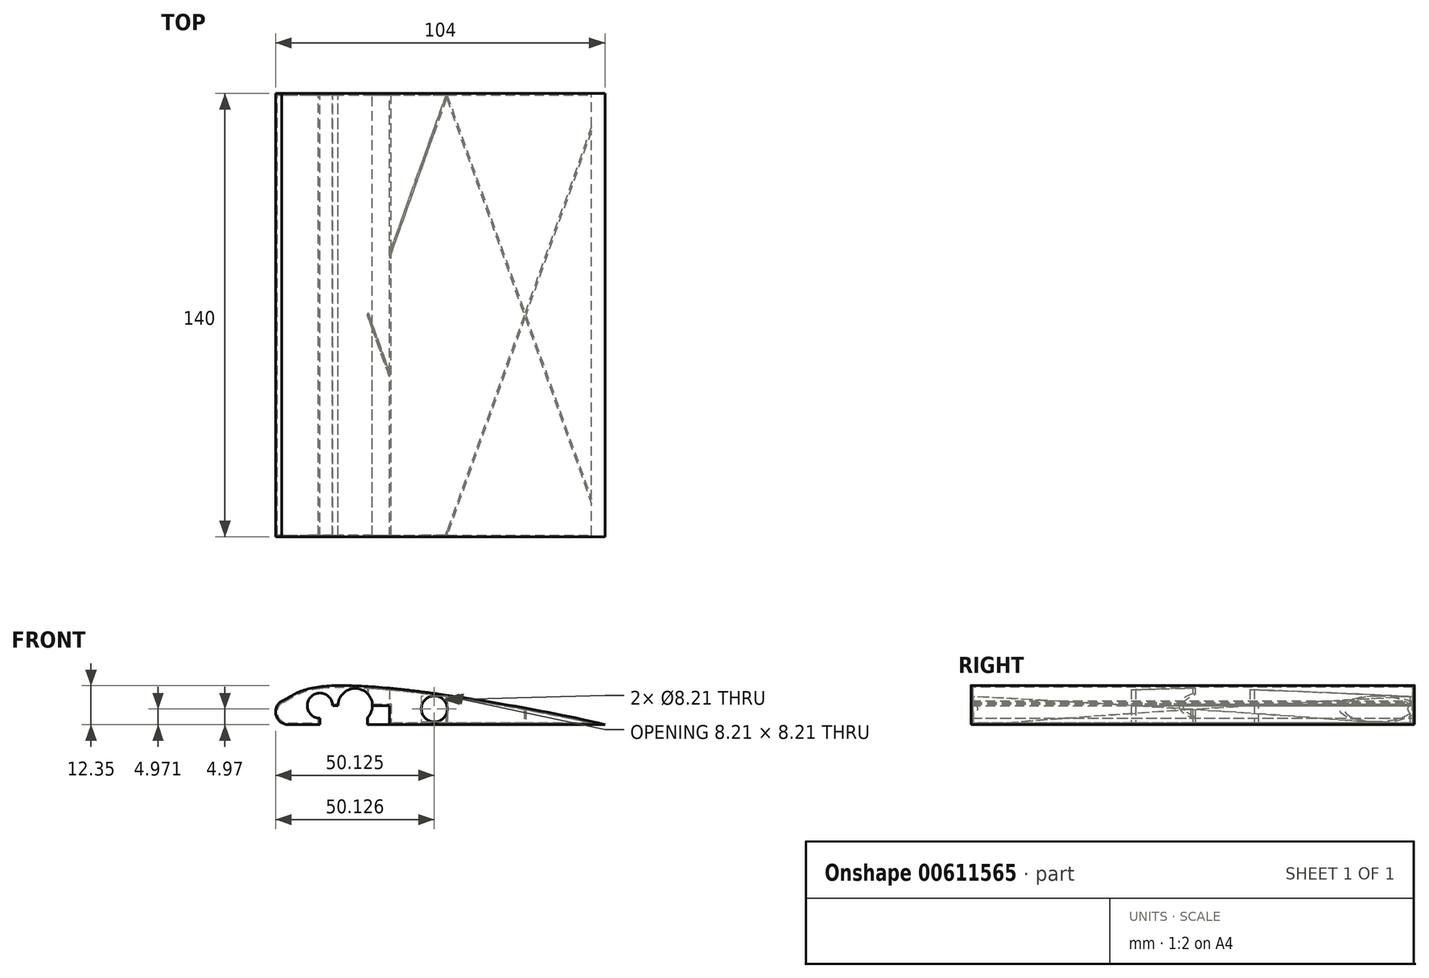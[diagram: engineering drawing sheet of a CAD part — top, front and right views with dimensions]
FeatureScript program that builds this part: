
annotation { "Feature Type Name" : "Feature", "Feature Type Description" : "" }
export const myFeature = defineFeature(function(context is Context, id is Id, definition is map)
    precondition{}
    {
        {
            var Q0;
            Q0=qCreatedBy(makeId("Front.planeOp"),FACE);
            var sketch = newSketch(context, id + "F0", { "sketchPlane" : qUnion([Q0])});
            skLineSegment(sketch, "E0", {"start": v(8.9, -4) * mm, "end": v(18.9, -4) * mm});
            skLineSegment(sketch, "E1", {"start": v(18.9, -4) * mm, "end": v(44.5, -4) * mm});
            skLineSegment(sketch, "E2", {"start": v(8.9, -4) * mm, "end": v(8.9, 4) * mm});
            skLineSegment(sketch, "E3", {"start": v(18.9, -4) * mm, "end": v(18.9, 8) * mm});
            skLineSegment(sketch, "E4", {"start": v(8.9, -4) * mm, "end": v(8.9, 0) * mm});
            skArc(sketch, "E5", {"start": v(8.9, -4) * mm, "mid": v(5.04, -1.04) * mm, "end": v(6.9, 3.46) * mm});
            skFitSpline(sketch, "E6", {"points": [v(6.9, 3.46) * mm, v(18.9, 8) * mm, v(108.9, -4) * mm], "startDerivative": vector(25.72, 9) * mm, "endDerivative": vector(55.93, -14.48) * mm});
            skLineSegment(sketch, "E7", {"start": v(44.5, -4) * mm, "end": v(108.9, -4) * mm});
            skLineSegment(sketch, "E8", {"start": v(44.5, -4) * mm, "end": v(40.83, -4) * mm});
            skLineSegment(sketch, "E9", {"start": v(40.83, -4) * mm, "end": v(40.83, 7.52) * mm});
            skCircle(sketch, "E10", {"center": v(8.9, 0) * mm, "radius": 4 * mm});
            skLineSegment(sketch, "E11", {"start": v(18.9, -4) * mm, "end": v(18.9, 2) * mm});
            skCircle(sketch, "E12", {"center": v(18.9, 2) * mm, "radius": 4 * mm});
            skLineSegment(sketch, "E13.right", {"start": v(55.04, 10.81) * mm, "end": v(55.04, -6.12) * mm});
            skLineSegment(sketch, "E14", {"start": v(18.9, 2) * mm, "end": v(30.05, 2) * mm});
            skLineSegment(sketch, "E15", {"start": v(30.05, 2) * mm, "end": v(40.83, 2) * mm});
            skLineSegment(sketch, "E16", {"start": v(40.83, 2) * mm, "end": v(55.04, 0.97) * mm});
            skCircle(sketch, "E17", {"center": v(30.05, 2) * mm, "radius": 5.42 * mm});
            skCircle(sketch, "E18", {"center": v(55.04, 0.97) * mm, "radius": 4.1 * mm});
            skLineSegment(sketch, "E19.bottom", {"start": v(-23.58, 40.57) * mm, "end": v(120.4, 40.57) * mm});
            skLineSegment(sketch, "E19.top", {"start": v(-23.58, -44.68) * mm, "end": v(120.4, -44.68) * mm});
            skLineSegment(sketch, "E19.left", {"start": v(-23.58, 40.57) * mm, "end": v(-23.58, -44.68) * mm});
            skLineSegment(sketch, "E19.right", {"start": v(120.4, 40.57) * mm, "end": v(120.4, -44.68) * mm});
            skSolve(sketch);
        }
        {
            var Q0;
            {var subQ1=sQuery(id+"F0.wireOp",EDGE,"E2");Q0=makeQuery(id+"F0.imprint","IMPRINT",FACE,{"disambiguationData":[TD([[makeQuery(id+"F0.imprint","IMPRINT",EDGE,{"derivedFrom":subQ1}),1.0]])]});}
            var Q1;
            {var subQ8=sQuery(id+"F0.wireOp",EDGE,"E0");Q1=makeQuery(id+"F0.imprint","IMPRINT",FACE,{"disambiguationData":[TD([[makeQuery(id+"F0.imprint","IMPRINT",EDGE,{"derivedFrom":subQ8}),1.0]])]});}
            var Q2;
            {var subQ1=sQuery(id+"F0.wireOp",EDGE,"E1");Q2=makeQuery(id+"F0.imprint","IMPRINT",FACE,{"disambiguationData":[TD([[makeQuery(id+"F0.imprint","IMPRINT",EDGE,{"derivedFrom":subQ1}),1.0]])]});}
            var Q3;
            {var subQ0=sQuery(id+"F0.wireOp",EDGE,"E7");Q3=makeQuery(id+"F0.imprint","IMPRINT",FACE,{"disambiguationData":[TD([[makeQuery(id+"F0.imprint","IMPRINT",EDGE,{"derivedFrom":subQ0}),1.0]])]});}
            var Q4;
            {var subQ1=sQuery(id+"F0.wireOp",EDGE,"E3");var subQ10=sQuery(id+"F0.wireOp",EDGE,"E6");var subQ12=makeQuery(id+"F0.imprint","INTERSECT",VERTEX,{"derivedFrom":[subQ1,subQ10]});Q4=makeQuery(id+"F0.imprint","IMPRINT",FACE,{"disambiguationData":[TD([[makeQuery(id+"F0.imprint","IMPRINT",EDGE,{"disambiguationData":[TD([[subQ12,1.0]])],"derivedFrom":subQ1}),-1.0]])]});}
            var Q5;
            {var subQ1=sQuery(id+"F0.wireOp",EDGE,"E6");var subQ5=sQuery(id+"F0.wireOp",EDGE,"E9");var subQ6=makeQuery(id+"F0.imprint","INTERSECT",VERTEX,{"derivedFrom":[subQ1,subQ5]});Q5=makeQuery(id+"F0.imprint","IMPRINT",FACE,{"disambiguationData":[TD([[makeQuery(id+"F0.imprint","IMPRINT",EDGE,{"disambiguationData":[TD([[subQ6,-1.0]])],"derivedFrom":subQ1}),-1.0]])]});}
            var Q6;
            {var subQ1=sQuery(id+"F0.wireOp",EDGE,"E8");Q6=makeQuery(id+"F0.imprint","IMPRINT",FACE,{"disambiguationData":[TD([[makeQuery(id+"F0.imprint","IMPRINT",EDGE,{"derivedFrom":subQ1}),-1.0]])]});}
            var Q7;
            {var subQ0=sQuery(id+"F0.wireOp",EDGE,"E2");Q7=makeQuery(id+"F0.imprint","IMPRINT",FACE,{"disambiguationData":[TD([[makeQuery(id+"F0.imprint","IMPRINT",EDGE,{"derivedFrom":subQ0}),-1.0]])]});}
            var Q8;
            {var subQ0=sQuery(id+"F0.wireOp",EDGE,"E15");var subQ1=sQuery(id+"F0.wireOp",EDGE,"E14");var subQ2=makeQuery(id+"F0.imprint","INTERSECT",VERTEX,{"derivedFrom":[subQ1,subQ0]});Q8=makeQuery(id+"F0.imprint","IMPRINT",FACE,{"disambiguationData":[TD([[makeQuery(id+"F0.imprint","IMPRINT",EDGE,{"disambiguationData":[TD([[subQ2,1.0]])],"derivedFrom":subQ1}),1.0]])]});}
            var Q9;
            {var subQ0=sQuery(id+"F0.wireOp",EDGE,"E15");var subQ1=sQuery(id+"F0.wireOp",EDGE,"E14");var subQ2=makeQuery(id+"F0.imprint","INTERSECT",VERTEX,{"derivedFrom":[subQ1,subQ0]});Q9=makeQuery(id+"F0.imprint","IMPRINT",FACE,{"disambiguationData":[TD([[makeQuery(id+"F0.imprint","IMPRINT",EDGE,{"disambiguationData":[TD([[subQ2,1.0]])],"derivedFrom":subQ1}),-1.0]])]});}
            var Q10;
            {var subQ1=sQuery(id+"F0.wireOp",EDGE,"E3");var subQ3=sQuery(id+"F0.wireOp",EDGE,"E12");var subQ4=makeQuery(id+"F0.imprint","INTERSECT",VERTEX,{"derivedFrom":[subQ1,subQ3]});Q10=makeQuery(id+"F0.imprint","IMPRINT",FACE,{"disambiguationData":[TD([[makeQuery(id+"F0.imprint","IMPRINT",EDGE,{"disambiguationData":[TD([[subQ4,-1.0]])],"derivedFrom":subQ3}),1.0]])]});}
            var Q11;
            {var subQ0=sQuery(id+"F0.wireOp",EDGE,"E16");var subQ1=sQuery(id+"F0.wireOp",EDGE,"E13.right");var subQ2=makeQuery(id+"F0.imprint","INTERSECT",VERTEX,{"derivedFrom":[subQ1,subQ0]});Q11=makeQuery(id+"F0.imprint","IMPRINT",FACE,{"disambiguationData":[TD([[makeQuery(id+"F0.imprint","IMPRINT",EDGE,{"disambiguationData":[TD([[subQ2,-1.0]])],"derivedFrom":subQ1}),-1.0]])]});}
            var Q12;
            {var subQ0=sQuery(id+"F0.wireOp",EDGE,"E13.right");var subQ1=makeQuery(id+"F0.imprint","INTERSECT",VERTEX,{"derivedFrom":[subQ0,sQuery(id+"F0.wireOp",EDGE,"E16")]});Q12=makeQuery(id+"F0.imprint","IMPRINT",FACE,{"disambiguationData":[TD([[makeQuery(id+"F0.imprint","IMPRINT",EDGE,{"disambiguationData":[TD([[subQ1,1.0]])],"derivedFrom":subQ0}),1.0]])]});}
            var Q13;
            {var subQ0=sQuery(id+"F0.wireOp",EDGE,"E16");var subQ1=sQuery(id+"F0.wireOp",EDGE,"E13.right");var subQ2=makeQuery(id+"F0.imprint","INTERSECT",VERTEX,{"derivedFrom":[subQ1,subQ0]});Q13=makeQuery(id+"F0.imprint","IMPRINT",FACE,{"disambiguationData":[TD([[makeQuery(id+"F0.imprint","IMPRINT",EDGE,{"disambiguationData":[TD([[subQ2,1.0]])],"derivedFrom":subQ1}),-1.0]])]});}
            var Q14;
            {var subQ1=sQuery(id+"F0.wireOp",EDGE,"E11");var subQ3=sQuery(id+"F0.wireOp",EDGE,"E12");var subQ4=makeQuery(id+"F0.imprint","INTERSECT",VERTEX,{"derivedFrom":[subQ1,subQ3]});Q14=makeQuery(id+"F0.imprint","IMPRINT",FACE,{"disambiguationData":[TD([[makeQuery(id+"F0.imprint","IMPRINT",EDGE,{"disambiguationData":[TD([[subQ4,-1.0]])],"derivedFrom":subQ3}),1.0]])]});}
            var Q15;
            {var subQ1=sQuery(id+"F0.wireOp",EDGE,"E3");var subQ3=sQuery(id+"F0.wireOp",EDGE,"E12");var subQ4=makeQuery(id+"F0.imprint","INTERSECT",VERTEX,{"derivedFrom":[subQ1,subQ3]});Q15=makeQuery(id+"F0.imprint","IMPRINT",FACE,{"disambiguationData":[TD([[makeQuery(id+"F0.imprint","IMPRINT",EDGE,{"disambiguationData":[TD([[subQ4,1.0]])],"derivedFrom":subQ3}),1.0]])]});}
            extrude(context, id + "F1", {"entities" : qUnion([Q0, Q1, Q2, Q3, Q4, Q5, Q6, Q7, Q8, Q9, Q10, Q11, Q12, Q13, Q14, Q15]), "depth" : 140 * mm, "offsetDistance" : 25 * mm});
        }
        {
            var Q0;
            Q0=makeQuery(id+"F1.opExtrude","CAP_FACE",FACE,{"disambiguationData":[OSD([sQuery(id+"F0.wireOp",EDGE,"E0"),sQuery(id+"F0.wireOp",EDGE,"E1"),sQuery(id+"F0.wireOp",EDGE,"E6"),sQuery(id+"F0.wireOp",EDGE,"E7"),sQuery(id+"F0.wireOp",EDGE,"E8"),sQuery(id+"F0.wireOp",EDGE,"E10"),sQuery(id+"F0.wireOp",EDGE,"E12"),sQuery(id+"F0.wireOp",EDGE,"E17"),sQuery(id+"F0.wireOp",EDGE,"E18")])],"isStart":false});
            var Q1;
            Q1=makeQuery(id+"F1.opExtrude","SWEPT_BODY",BODY,{"disambiguationData":[OSD([sQuery(id+"F0.wireOp",EDGE,"E0"),sQuery(id+"F0.wireOp",EDGE,"E1"),sQuery(id+"F0.wireOp",EDGE,"E6"),sQuery(id+"F0.wireOp",EDGE,"E7"),sQuery(id+"F0.wireOp",EDGE,"E8"),sQuery(id+"F0.wireOp",EDGE,"E10"),sQuery(id+"F0.wireOp",EDGE,"E12"),sQuery(id+"F0.wireOp",EDGE,"E17"),sQuery(id+"F0.wireOp",EDGE,"E18")])]});
            shell(context, id + "F2", {"isHollow" : true, "entities" : qUnion([Q0]), "parts" : qUnion([Q1]), "thickness" : 0.5 * mm});
        }
        {
            var Q0;
            Q0=makeQuery(id+"F1.opExtrude","SWEPT_FACE",FACE,{"disambiguationData":[OSD([sQuery(id+"F0.wireOp",EDGE,"E0"),sQuery(id+"F0.wireOp",EDGE,"E1"),sQuery(id+"F0.wireOp",EDGE,"E7"),sQuery(id+"F0.wireOp",EDGE,"E8")])]});
            var sketch = newSketch(context, id + "F3", { "sketchPlane" : qUnion([Q0])});
            skLineSegment(sketch, "E20", {"start": v(8.9, 140) * mm, "end": v(58.9, 140) * mm});
            skLineSegment(sketch, "E21", {"start": v(58.9, 140) * mm, "end": v(58.9, 0) * mm});
            skLineSegment(sketch, "E22", {"start": v(58.9, 0) * mm, "end": v(8.9, 140) * mm});
            skLineSegment(sketch, "E23", {"start": v(108.9, 140) * mm, "end": v(58.9, 0) * mm});
            skLineSegment(sketch, "E24", {"start": v(8.9, 0) * mm, "end": v(58.9, 140) * mm});
            skLineSegment(sketch, "E25", {"start": v(58.9, 140) * mm, "end": v(108.9, 0) * mm});
            skLineSegment(sketch, "E26", {"start": v(58.9, 140) * mm, "end": v(58.4, 140) * mm});
            skLineSegment(sketch, "E27", {"start": v(58.4, 140) * mm, "end": v(58.9, 140) * mm});
            skLineSegment(sketch, "E28", {"start": v(58.4, 140) * mm, "end": v(108.4, 0) * mm});
            skLineSegment(sketch, "E29.MirrorCS", {"start": v(59.4, 140) * mm, "end": v(9.4, 0) * mm});
            skLineSegment(sketch, "E30.MirrorCS", {"start": v(59.4, 140) * mm, "end": v(58.9, 140) * mm});
            skLineSegment(sketch, "E31", {"start": v(8.9, 140) * mm, "end": v(9.4, 140) * mm});
            skLineSegment(sketch, "E32", {"start": v(9.4, 140) * mm, "end": v(59.4, 0) * mm});
            skLineSegment(sketch, "E33.MirrorCS", {"start": v(108.4, 140) * mm, "end": v(58.4, 0) * mm});
            skLineSegment(sketch, "E34.MirrorCS", {"start": v(108.9, 140) * mm, "end": v(108.4, 140) * mm});
            skSolve(sketch);
        }
        {
            var Q0;
            {var subQ0=sQuery(id+"F3.wireOp",EDGE,"E27");Q0=makeQuery(id+"F3.imprint","IMPRINT",FACE,{"disambiguationData":[TD([[makeQuery(id+"F3.imprint","IMPRINT",EDGE,{"derivedFrom":subQ0}),-1.0]])]});}
            var Q1;
            {var subQ0=sQuery(id+"F3.wireOp",EDGE,"E30.MirrorCS");Q1=makeQuery(id+"F3.imprint","IMPRINT",FACE,{"disambiguationData":[TD([[makeQuery(id+"F3.imprint","IMPRINT",EDGE,{"derivedFrom":subQ0}),-1.0]])]});}
            var Q2;
            {var subQ0=sQuery(id+"F3.wireOp",EDGE,"E24");var subQ3=sQuery(id+"F3.wireOp",EDGE,"E28");var subQ5=makeQuery(id+"F3.imprint","INTERSECT",VERTEX,{"derivedFrom":[subQ0,subQ3]});Q2=makeQuery(id+"F3.imprint","IMPRINT",FACE,{"disambiguationData":[TD([[makeQuery(id+"F3.imprint","IMPRINT",EDGE,{"disambiguationData":[TD([[subQ5,-1.0]])],"derivedFrom":subQ3}),1.0]])]});}
            var Q3;
            {var subQ0=sQuery(id+"F3.wireOp",EDGE,"E25");var subQ3=sQuery(id+"F3.wireOp",EDGE,"E29.MirrorCS");var subQ5=makeQuery(id+"F3.imprint","INTERSECT",VERTEX,{"derivedFrom":[subQ0,subQ3]});Q3=makeQuery(id+"F3.imprint","IMPRINT",FACE,{"disambiguationData":[TD([[makeQuery(id+"F3.imprint","IMPRINT",EDGE,{"disambiguationData":[TD([[subQ5,-1.0]])],"derivedFrom":subQ3}),-1.0]])]});}
            var Q4;
            {var subQ0=sQuery(id+"F3.wireOp",EDGE,"E22");var subQ3=sQuery(id+"F3.wireOp",EDGE,"E33.MirrorCS");var subQ5=makeQuery(id+"F3.imprint","INTERSECT",VERTEX,{"derivedFrom":[subQ0,subQ3]});Q4=makeQuery(id+"F3.imprint","IMPRINT",FACE,{"disambiguationData":[TD([[makeQuery(id+"F3.imprint","IMPRINT",EDGE,{"disambiguationData":[TD([[subQ5,1.0]])],"derivedFrom":subQ3}),1.0]])]});}
            var Q5;
            {var subQ0=sQuery(id+"F3.wireOp",EDGE,"E23");var subQ3=sQuery(id+"F3.wireOp",EDGE,"E32");var subQ5=makeQuery(id+"F3.imprint","INTERSECT",VERTEX,{"derivedFrom":[subQ0,subQ3]});Q5=makeQuery(id+"F3.imprint","IMPRINT",FACE,{"disambiguationData":[TD([[makeQuery(id+"F3.imprint","IMPRINT",EDGE,{"disambiguationData":[TD([[subQ5,1.0]])],"derivedFrom":subQ3}),-1.0]])]});}
            var Q6;
            {var subQ0=sQuery(id+"F3.wireOp",EDGE,"E31");Q6=makeQuery(id+"F3.imprint","IMPRINT",FACE,{"disambiguationData":[TD([[makeQuery(id+"F3.imprint","IMPRINT",EDGE,{"derivedFrom":subQ0}),-1.0]])]});}
            var Q7;
            {var subQ0=sQuery(id+"F3.wireOp",EDGE,"E34.MirrorCS");Q7=makeQuery(id+"F3.imprint","IMPRINT",FACE,{"disambiguationData":[TD([[makeQuery(id+"F3.imprint","IMPRINT",EDGE,{"derivedFrom":subQ0}),-1.0]])]});}
            var Q8;
            {var subQ0=sQuery(id+"F3.wireOp",EDGE,"E33.MirrorCS");var subQ1=sQuery(id+"F3.wireOp",EDGE,"E22");var subQ2=makeQuery(id+"F3.imprint","INTERSECT",VERTEX,{"derivedFrom":[subQ1,subQ0]});Q8=makeQuery(id+"F3.imprint","IMPRINT",FACE,{"disambiguationData":[TD([[makeQuery(id+"F3.imprint","IMPRINT",EDGE,{"disambiguationData":[TD([[subQ2,-1.0]])],"derivedFrom":subQ1}),-1.0]])]});}
            var Q9;
            {var subQ0=sQuery(id+"F3.wireOp",EDGE,"E29.MirrorCS");var subQ1=sQuery(id+"F3.wireOp",EDGE,"E22");var subQ2=makeQuery(id+"F3.imprint","INTERSECT",VERTEX,{"derivedFrom":[subQ1,subQ0]});Q9=makeQuery(id+"F3.imprint","IMPRINT",FACE,{"disambiguationData":[TD([[makeQuery(id+"F3.imprint","IMPRINT",EDGE,{"disambiguationData":[TD([[subQ2,-1.0]])],"derivedFrom":subQ1}),-1.0]])]});}
            var Q10;
            {var subQ0=sQuery(id+"F3.wireOp",EDGE,"E25");var subQ1=sQuery(id+"F3.wireOp",EDGE,"E23");var subQ2=makeQuery(id+"F3.imprint","INTERSECT",VERTEX,{"derivedFrom":[subQ1,subQ0]});Q10=makeQuery(id+"F3.imprint","IMPRINT",FACE,{"disambiguationData":[TD([[makeQuery(id+"F3.imprint","IMPRINT",EDGE,{"disambiguationData":[TD([[subQ2,-1.0]])],"derivedFrom":subQ1}),-1.0]])]});}
            var Q11;
            {var subQ0=sQuery(id+"F3.wireOp",EDGE,"E28");var subQ1=sQuery(id+"F3.wireOp",EDGE,"E23");var subQ2=makeQuery(id+"F3.imprint","INTERSECT",VERTEX,{"derivedFrom":[subQ1,subQ0]});Q11=makeQuery(id+"F3.imprint","IMPRINT",FACE,{"disambiguationData":[TD([[makeQuery(id+"F3.imprint","IMPRINT",EDGE,{"disambiguationData":[TD([[subQ2,-1.0]])],"derivedFrom":subQ1}),-1.0]])]});}
            var Q12;
            {var subQ0=sQuery(id+"F3.wireOp",EDGE,"E29.MirrorCS");var subQ1=sQuery(id+"F3.wireOp",EDGE,"E25");var subQ2=makeQuery(id+"F3.imprint","INTERSECT",VERTEX,{"derivedFrom":[subQ1,subQ0]});Q12=makeQuery(id+"F3.imprint","IMPRINT",FACE,{"disambiguationData":[TD([[makeQuery(id+"F3.imprint","IMPRINT",EDGE,{"disambiguationData":[TD([[subQ2,-1.0]])],"derivedFrom":subQ1}),-1.0]])]});}
            var Q13;
            {var subQ0=sQuery(id+"F3.wireOp",EDGE,"E32");var subQ1=sQuery(id+"F3.wireOp",EDGE,"E24");var subQ2=makeQuery(id+"F3.imprint","INTERSECT",VERTEX,{"derivedFrom":[subQ1,subQ0]});Q13=makeQuery(id+"F3.imprint","IMPRINT",FACE,{"disambiguationData":[TD([[makeQuery(id+"F3.imprint","IMPRINT",EDGE,{"disambiguationData":[TD([[subQ2,-1.0]])],"derivedFrom":subQ1}),-1.0]])]});}
            var Q14;
            {var subQ0=sQuery(id+"F3.wireOp",EDGE,"E29.MirrorCS");var subQ1=sQuery(id+"F3.wireOp",EDGE,"E22");var subQ2=makeQuery(id+"F3.imprint","INTERSECT",VERTEX,{"derivedFrom":[subQ1,subQ0]});Q14=makeQuery(id+"F3.imprint","IMPRINT",FACE,{"disambiguationData":[TD([[makeQuery(id+"F3.imprint","IMPRINT",EDGE,{"disambiguationData":[TD([[subQ2,-1.0]])],"derivedFrom":subQ1}),1.0]])]});}
            var Q15;
            {var subQ0=sQuery(id+"F3.wireOp",EDGE,"E25");var subQ1=sQuery(id+"F3.wireOp",EDGE,"E23");var subQ2=makeQuery(id+"F3.imprint","INTERSECT",VERTEX,{"derivedFrom":[subQ1,subQ0]});Q15=makeQuery(id+"F3.imprint","IMPRINT",FACE,{"disambiguationData":[TD([[makeQuery(id+"F3.imprint","IMPRINT",EDGE,{"disambiguationData":[TD([[subQ2,-1.0]])],"derivedFrom":subQ1}),1.0]])]});}
            extrude(context, id + "F4", {"entities" : qUnion([Q0, Q1, Q2, Q3, Q4, Q5, Q6, Q7, Q8, Q9, Q10, Q11, Q12, Q13, Q14, Q15]), "operationType" : NewBodyOperationType.ADD, "oppositeDirection" : true, "depth" : 25 * mm, "offsetDistance" : 25 * mm});
        }
        {
            var Q0;
            {var subQ0=sQuery(id+"F0.wireOp",EDGE,"E15");var subQ1=sQuery(id+"F0.wireOp",EDGE,"E14");var subQ2=makeQuery(id+"F0.imprint","INTERSECT",VERTEX,{"derivedFrom":[subQ1,subQ0]});Q0=makeQuery(id+"F0.imprint","IMPRINT",FACE,{"disambiguationData":[TD([[makeQuery(id+"F0.imprint","IMPRINT",EDGE,{"disambiguationData":[TD([[subQ2,1.0]])],"derivedFrom":subQ1}),1.0]])]});}
            var Q1;
            {var subQ1=sQuery(id+"F0.wireOp",EDGE,"E3");var subQ3=sQuery(id+"F0.wireOp",EDGE,"E12");var subQ4=makeQuery(id+"F0.imprint","INTERSECT",VERTEX,{"derivedFrom":[subQ1,subQ3]});Q1=makeQuery(id+"F0.imprint","IMPRINT",FACE,{"disambiguationData":[TD([[makeQuery(id+"F0.imprint","IMPRINT",EDGE,{"disambiguationData":[TD([[subQ4,-1.0]])],"derivedFrom":subQ3}),1.0]])]});}
            var Q2;
            {var subQ1=sQuery(id+"F0.wireOp",EDGE,"E11");var subQ3=sQuery(id+"F0.wireOp",EDGE,"E12");var subQ4=makeQuery(id+"F0.imprint","INTERSECT",VERTEX,{"derivedFrom":[subQ1,subQ3]});Q2=makeQuery(id+"F0.imprint","IMPRINT",FACE,{"disambiguationData":[TD([[makeQuery(id+"F0.imprint","IMPRINT",EDGE,{"disambiguationData":[TD([[subQ4,-1.0]])],"derivedFrom":subQ3}),1.0]])]});}
            var Q3;
            {var subQ1=sQuery(id+"F0.wireOp",EDGE,"E3");var subQ3=sQuery(id+"F0.wireOp",EDGE,"E12");var subQ4=makeQuery(id+"F0.imprint","INTERSECT",VERTEX,{"derivedFrom":[subQ1,subQ3]});Q3=makeQuery(id+"F0.imprint","IMPRINT",FACE,{"disambiguationData":[TD([[makeQuery(id+"F0.imprint","IMPRINT",EDGE,{"disambiguationData":[TD([[subQ4,1.0]])],"derivedFrom":subQ3}),1.0]])]});}
            var Q4;
            {var subQ0=sQuery(id+"F0.wireOp",EDGE,"E13.right");var subQ1=makeQuery(id+"F0.imprint","INTERSECT",VERTEX,{"derivedFrom":[subQ0,sQuery(id+"F0.wireOp",EDGE,"E16")]});Q4=makeQuery(id+"F0.imprint","IMPRINT",FACE,{"disambiguationData":[TD([[makeQuery(id+"F0.imprint","IMPRINT",EDGE,{"disambiguationData":[TD([[subQ1,1.0]])],"derivedFrom":subQ0}),1.0]])]});}
            var Q5;
            {var subQ0=sQuery(id+"F0.wireOp",EDGE,"E16");var subQ1=sQuery(id+"F0.wireOp",EDGE,"E13.right");var subQ2=makeQuery(id+"F0.imprint","INTERSECT",VERTEX,{"derivedFrom":[subQ1,subQ0]});Q5=makeQuery(id+"F0.imprint","IMPRINT",FACE,{"disambiguationData":[TD([[makeQuery(id+"F0.imprint","IMPRINT",EDGE,{"disambiguationData":[TD([[subQ2,-1.0]])],"derivedFrom":subQ1}),-1.0]])]});}
            var Q6;
            {var subQ0=sQuery(id+"F0.wireOp",EDGE,"E16");var subQ1=sQuery(id+"F0.wireOp",EDGE,"E13.right");var subQ2=makeQuery(id+"F0.imprint","INTERSECT",VERTEX,{"derivedFrom":[subQ1,subQ0]});Q6=makeQuery(id+"F0.imprint","IMPRINT",FACE,{"disambiguationData":[TD([[makeQuery(id+"F0.imprint","IMPRINT",EDGE,{"disambiguationData":[TD([[subQ2,1.0]])],"derivedFrom":subQ1}),-1.0]])]});}
            var Q7;
            {var subQ0=sQuery(id+"F0.wireOp",EDGE,"E15");var subQ1=sQuery(id+"F0.wireOp",EDGE,"E14");var subQ2=makeQuery(id+"F0.imprint","INTERSECT",VERTEX,{"derivedFrom":[subQ1,subQ0]});Q7=makeQuery(id+"F0.imprint","IMPRINT",FACE,{"disambiguationData":[TD([[makeQuery(id+"F0.imprint","IMPRINT",EDGE,{"disambiguationData":[TD([[subQ2,1.0]])],"derivedFrom":subQ1}),-1.0]])]});}
            var Q8;
            {var subQ11=sQuery(id+"F0.wireOp",EDGE,"E0");Q8=makeQuery(id+"F0.imprint","IMPRINT",FACE,{"disambiguationData":[TD([[makeQuery(id+"F0.imprint","IMPRINT",EDGE,{"derivedFrom":subQ11}),-1.0]])]});}
            extrude(context, id + "F5", {"entities" : qUnion([Q0, Q1, Q2, Q3, Q4, Q5, Q6, Q7, Q8]), "operationType" : NewBodyOperationType.REMOVE, "depth" : 1000 * mm, "offsetDistance" : 25 * mm});
        }
    });
